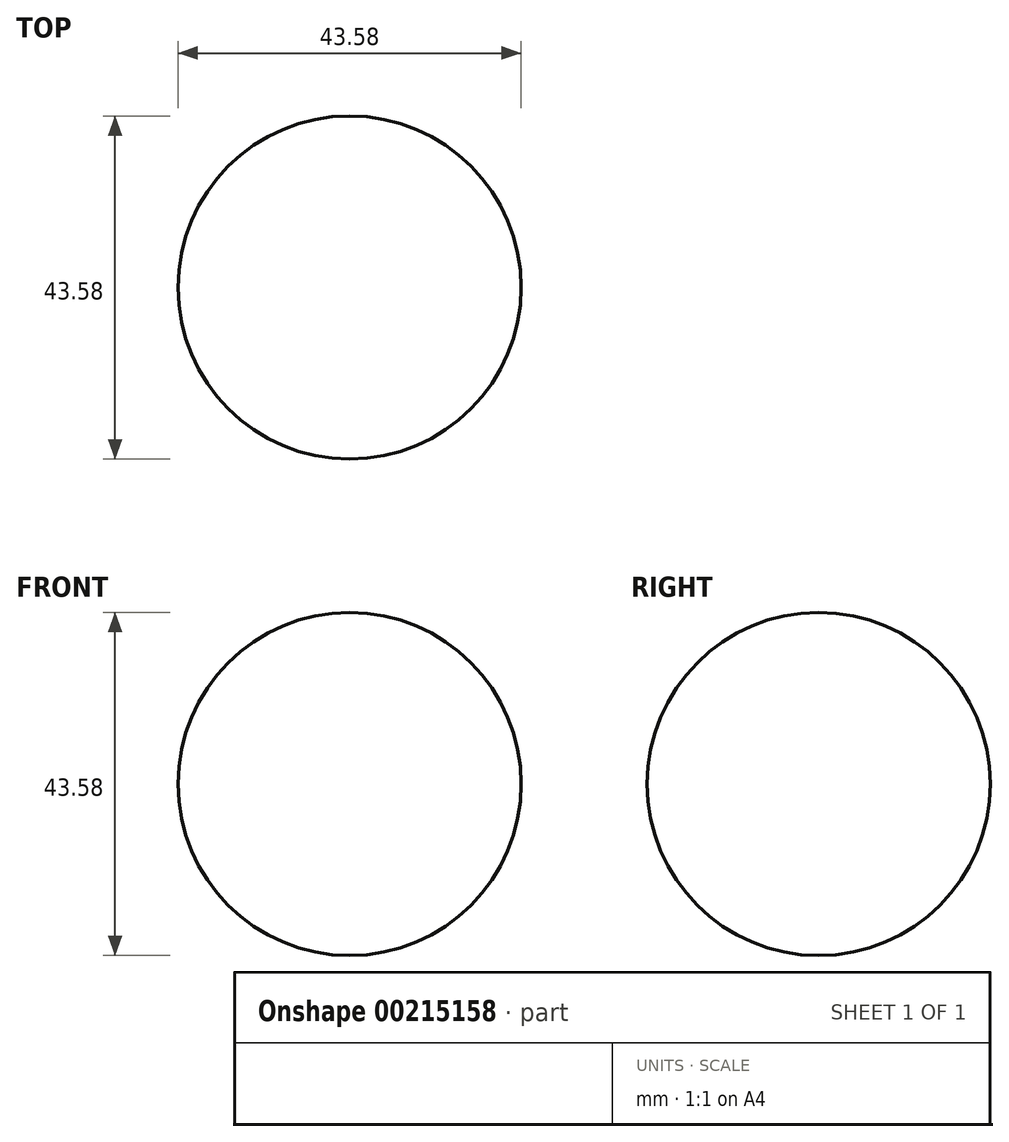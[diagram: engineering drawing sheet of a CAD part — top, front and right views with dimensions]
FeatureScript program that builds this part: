
annotation { "Feature Type Name" : "Feature", "Feature Type Description" : "" }
export const myFeature = defineFeature(function(context is Context, id is Id, definition is map)
    precondition{}
    {
        {
            var Q0;
            Q0=qCreatedBy(makeId("Top.planeOp"),FACE);
            var sketch = newSketch(context, id + "F0", { "sketchPlane" : qUnion([Q0])});
            skArc(sketch, "E0", {"start": v(21.8, 0) * mm, "mid": v(0, 21.8) * mm, "end": v(-21.8, 0) * mm});
            skLineSegment(sketch, "E1", {"start": v(0, 0) * mm, "end": v(21.8, 0) * mm});
            skLineSegment(sketch, "E2", {"start": v(21.8, 0) * mm, "end": v(-21.8, 0) * mm});
            skSolve(sketch);
        }
        {
            var Q0;
            {var subQ0=sQuery(id+"F0.wireOp",EDGE,"E0");Q0=makeQuery(id+"F0.imprint","IMPRINT",FACE,{"disambiguationData":[TD([[makeQuery(id+"F0.imprint","IMPRINT",EDGE,{"derivedFrom":subQ0}),1.0]])]});}
            var Q1;
            Q1=sQuery(id+"F0.wireOp",EDGE,"E0");
            var Q2;
            Q2=sQuery(id+"F0.wireOp",EDGE,"E2");
            revolve(context, id + "F1", {"entities" : qUnion([Q0]), "surfaceEntities" : qUnion([Q1]), "axis" : qUnion([Q2]), "revolveType" : RevolveType.FULL});
        }
    });
